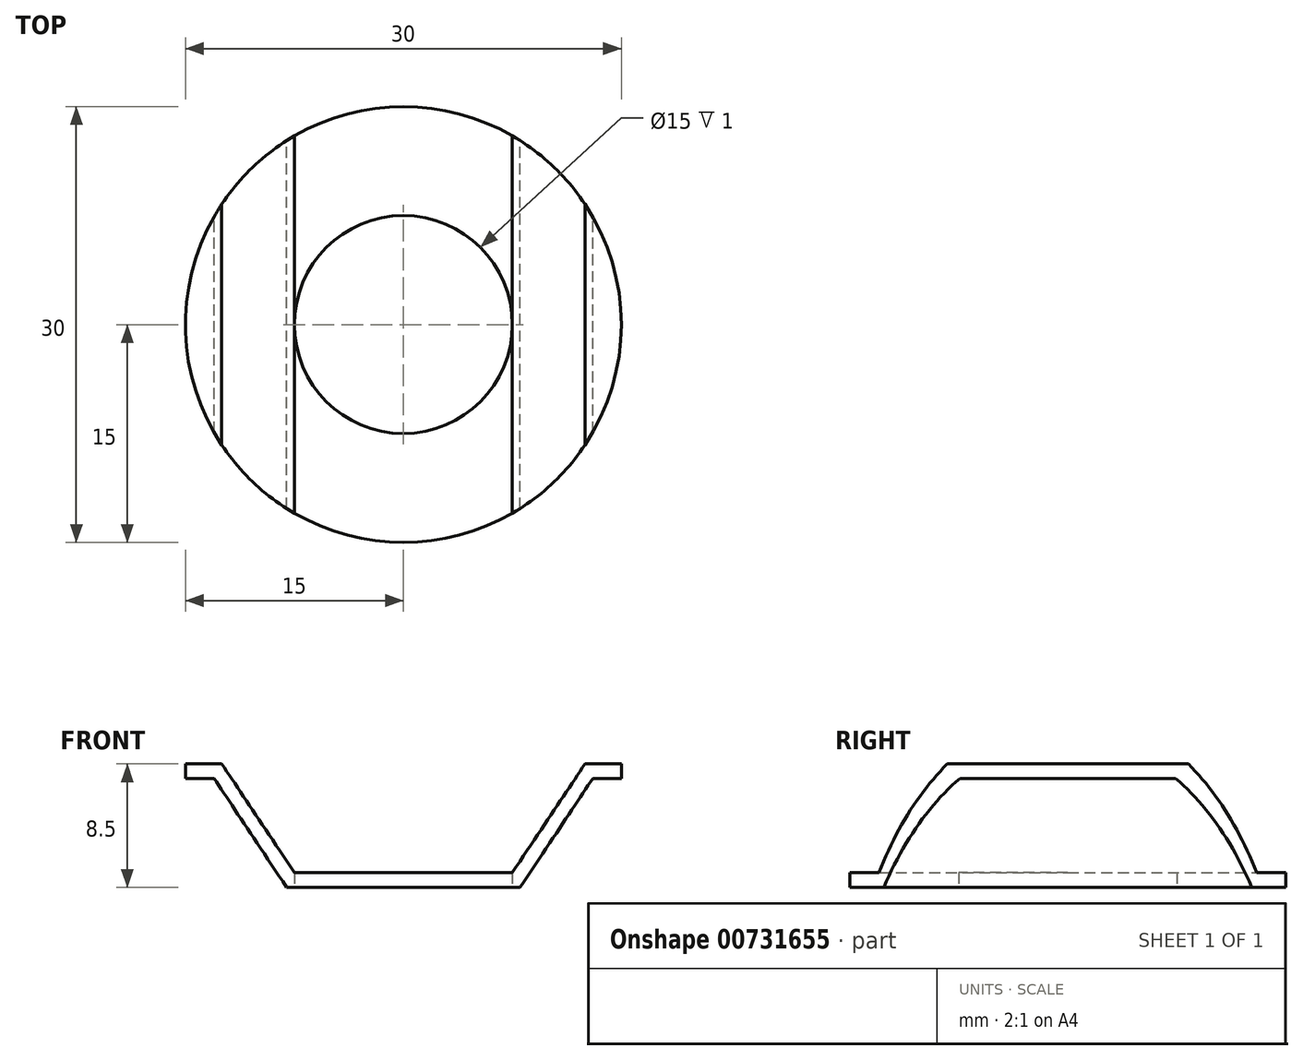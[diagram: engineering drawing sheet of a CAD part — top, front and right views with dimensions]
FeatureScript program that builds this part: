
annotation { "Feature Type Name" : "Feature", "Feature Type Description" : "" }
export const myFeature = defineFeature(function(context is Context, id is Id, definition is map)
    precondition{}
    {
        {
            var Q0;
            Q0=qCreatedBy(makeId("Front.planeOp"),FACE);
            var sketch = newSketch(context, id + "F0", { "sketchPlane" : qUnion([Q0])});
            skLineSegment(sketch, "E0", {"start": v(0, 0) * mm, "end": v(-7.5, 0) * mm});
            skLineSegment(sketch, "E1", {"start": v(-7.5, 0) * mm, "end": v(-12.5, 7.5) * mm});
            skLineSegment(sketch, "E2", {"start": v(-12.5, 7.5) * mm, "end": v(-15, 7.5) * mm});
            skLineSegment(sketch, "E3.0", {"start": v(-13.04, 6.5) * mm, "end": v(-15, 6.5) * mm});
            skLineSegment(sketch, "E3.1", {"start": v(-8.04, -1) * mm, "end": v(-13.04, 6.5) * mm});
            skLineSegment(sketch, "E3.2", {"start": v(0, -1) * mm, "end": v(-8.04, -1) * mm});
            skLineSegment(sketch, "E4", {"start": v(-15, 6.5) * mm, "end": v(-15, 7.5) * mm});
            skLineSegment(sketch, "E5", {"start": v(0, -1) * mm, "end": v(0, 0) * mm});
            skLineSegment(sketch, "E6.MirrorCS", {"start": v(0, 0) * mm, "end": v(7.5, 0) * mm});
            skLineSegment(sketch, "E7.MirrorCS", {"start": v(0, -1) * mm, "end": v(8.04, -1) * mm});
            skLineSegment(sketch, "E8.MirrorCS", {"start": v(7.5, 0) * mm, "end": v(12.5, 7.5) * mm});
            skLineSegment(sketch, "E9.MirrorCS", {"start": v(8.04, -1) * mm, "end": v(13.04, 6.5) * mm});
            skLineSegment(sketch, "E10.MirrorCS", {"start": v(12.5, 7.5) * mm, "end": v(15, 7.5) * mm});
            skLineSegment(sketch, "E11.MirrorCS", {"start": v(13.04, 6.5) * mm, "end": v(15, 6.5) * mm});
            skLineSegment(sketch, "E12.MirrorCS", {"start": v(15, 6.5) * mm, "end": v(15, 7.5) * mm});
            skSolve(sketch);
        }
        {
            var Q0;
            Q0=qSketchRegion(id+"F0",true);
            extrude(context, id + "F1", {"entities" : qUnion([Q0]), "depth" : 30 * mm, "offsetDistance" : 25 * mm});
        }
        {
            var Q0;
            Q0=qCreatedBy(makeId("Top.planeOp"),FACE);
            var sketch = newSketch(context, id + "F2", { "sketchPlane" : qUnion([Q0])});
            skCircle(sketch, "E13", {"center": v(0, -15) * mm, "radius": 15 * mm});
            skCircle(sketch, "E14.0", {"center": v(0, -15) * mm, "radius": 7.5 * mm});
            skSolve(sketch);
        }
        {
            var Q0;
            Q0=qSketchRegion(id+"F2",true);
            extrude(context, id + "F3", {"entities" : qUnion([Q0]), "operationType" : NewBodyOperationType.INTERSECT, "endBound" : BoundingType.THROUGH_ALL, "depth" : 25 * mm, "offsetDistance" : 25 * mm, "hasSecondDirection" : true, "secondDirectionOppositeDirection" : true, "secondDirectionDepth" : 25 * mm});
        }
    });
